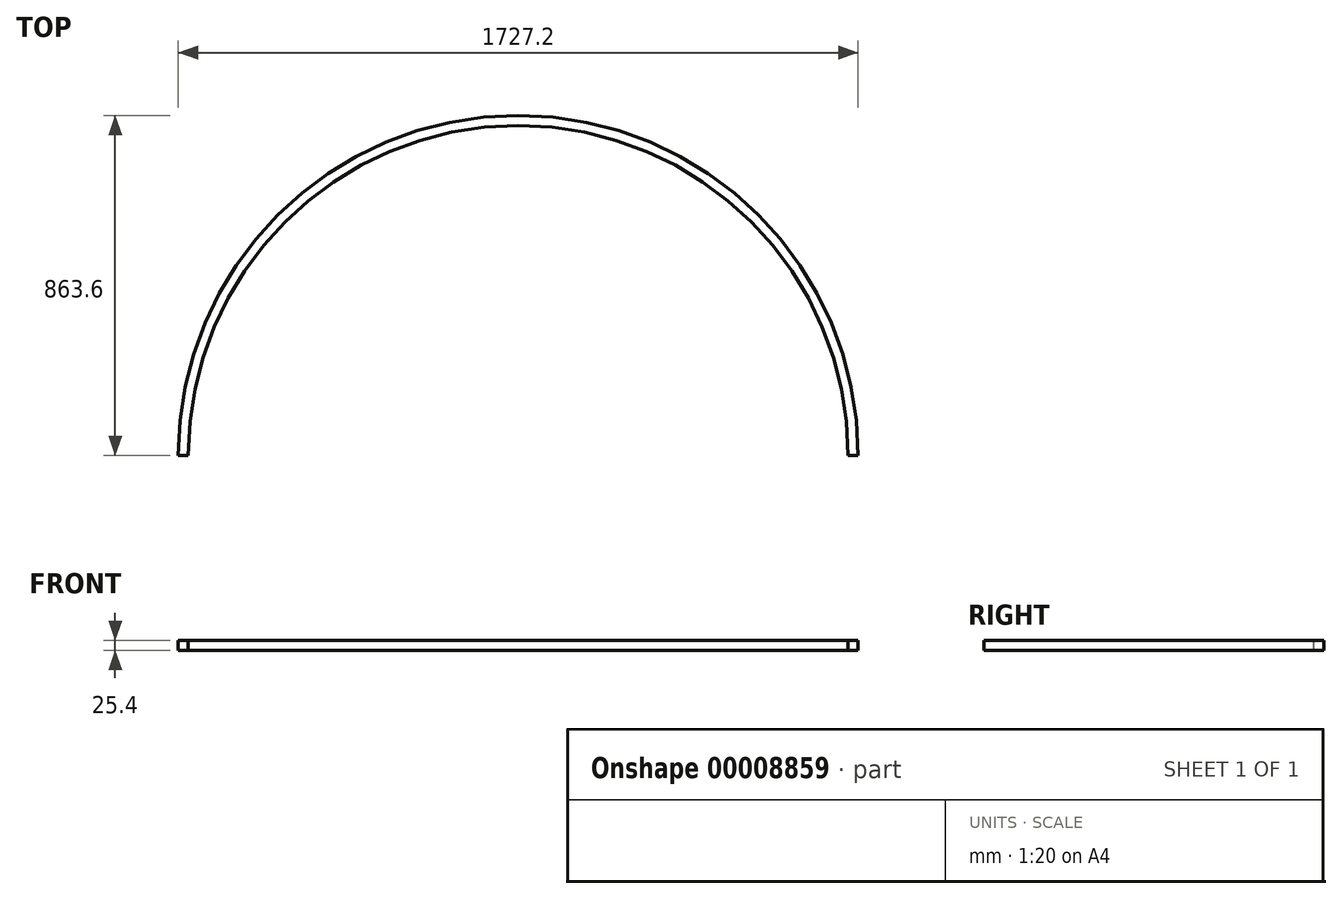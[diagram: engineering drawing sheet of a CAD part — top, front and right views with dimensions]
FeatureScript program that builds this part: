
annotation { "Feature Type Name" : "Feature", "Feature Type Description" : "" }
export const myFeature = defineFeature(function(context is Context, id is Id, definition is map)
    precondition{}
    {
        {
            var Q0;
            Q0=qCreatedBy(makeId("Front.planeOp"),FACE);
            var sketch = newSketch(context, id + "F0", { "sketchPlane" : qUnion([Q0])});
            skLineSegment(sketch, "E0.bottom", {"start": v(-13.04, 10.83) * mm, "end": v(12.36, 10.83) * mm});
            skLineSegment(sketch, "E0.top", {"start": v(-13.04, -14.57) * mm, "end": v(12.36, -14.57) * mm});
            skLineSegment(sketch, "E0.left", {"start": v(-13.04, 10.83) * mm, "end": v(-13.04, -14.57) * mm});
            skLineSegment(sketch, "E0.right", {"start": v(12.36, 10.83) * mm, "end": v(12.36, -14.57) * mm});
            skLineSegment(sketch, "E1", {"start": v(850.56, 19.21) * mm, "end": v(850.56, -34.27) * mm, "construction": true});
            skSolve(sketch);
        }
        {
            var Q0;
            Q0=makeQuery(id+"F0.imprint","IMPRINT",FACE,{"disambiguationData":[TD([[makeQuery(id+"F0.imprint","IMPRINT",EDGE,{"derivedFrom":sQuery(id+"F0.wireOp",EDGE,"E0.bottom")}),-1.0]])]});
            var Q1;
            Q1=sQuery(id+"F0.wireOp",EDGE,"E1");
            revolve(context, id + "F1", {"entities" : qUnion([Q0]), "axis" : qUnion([Q1]), "revolveType" : RevolveType.ONE_DIRECTION, "angle" : 180 * degree});
        }
    });
